# Revit family: PRD_AR_ShwrFttngsPckg_F5EShowerPanel_F5EV2008
name_source: partatom
category: Plumbing Fixtures
units: mm (PartAtom-declared; Revit-internal decimal feet)

## family parameters
Cut with Voids When Loaded = No
Enable Cutting in Views = No
Host = Face
Maintain Annotation Orientation = No
OmniClass Number = 23.45.05.14.17.11
OmniClass Title = Shower Compartments
Part Type = Normal
Room Calculation Point = No
Round Connector Dimension = Use Diameter
Shared = No

## types (1)
- F5EV2008
    AccentColour = chrome-look (glossy)
    AdditionalConnections = No
    AdjustableFlowTime = Yes
    Adjustment = No
    AssetType = Fixed
    BIMObjectName = PRD_AR_ ShowerFittingsPackage_F5EShowerPanel_F5EV2008
    BasicColour = stainless steel-look
    BodyMaterial = PRD_AR_StainlessSteel_SatinFinished
    Category = Pr_40_20_87_75, Shower fittings package
    Circulation = No
    Color = stainless steel-look
    CompatibleA3000Open = Yes
    ConnectionWithPayWaterDispenser = via electronic module
    DN = 15  [stored 0.0492126 ft]
    Default Elevation = 1200 mm
    Description = F5E - A3000 open shower panel made of stainless steel for wall mounting with straight-way valve and connecting nozzles for shower head. Electronically controlled, for connection from the rear to pre-mixed hot or cold water. Connecting nozzles for the required additional DN 15 KWC shower head with pre-fitted flow regulator 9.0 l/min. Housing made of stainless steel, single-piece enclosed, including safety screws. With solenoid valve, piezo push-button with start/stop function, waterproof electronic module, electric T-junction for connection to system cable, connecting hose with lockable water flow regulator and strainer. Activated hygiene flushing 24 hours after the last activity. With facility for parameterization, cleaning deactivation and communication via ECC2 function controller, 24 V DC.
    DiameterNominal = DN 15
    DrainSize = 15 mm  [stored 0.0492126 ft]
    Export Type to IFC As = IfcSanitaryTerminalType
    Features = For connection from the rear to pre-mixed hot or cold water. Dimensions of housing 232 x 1160 x 90 mm. Shower head must be ordered separately.
    Finish = Satin finished
    Flow = 0.2 L/s
    ForHandShower = No
    FunctionalPrinciple = Electronic self-closing
    HasTray = No
    HygieneFlushing = Yes
    IfcExportAs = IfcSanitaryTerminalType
    IfcExportType = SHOWER
    InletSize = G 1/2 A
    LockingMechanism = Top section, non-ceramic
    Manufacturer = KWC Group Management AG
    ManufacturerName = KWC Group Management AG
    ManufacturerURL = www.kwc-professional.com
    Material = stainless steel
    MaterialCasing = stainless steel
    MaterialCodeCasing = 1.4301 Chrome Nickel steel V2A
    MaterialFitting = brass-look
    MaximumFlowTime = 6500 Seconds
    MinimumFlowPressure = 1 bar
    MinimumFlowTime = 1 Seconds
    Model = F5EV2008
    ModelNumber = 2030070434
    ModelReference = F5EV2008
    NBSDescription = Shower fittings package
    NBSReference = 45-35-70/330
    Name = F5E Shower panel F5EV2008
    NominalDepth = 90 mm  [stored 0.295276 ft]
    NominalHeight = 1160 mm  [stored 3.80577 ft]
    NominalLength = 1160 mm  [stored 3.80577 ft]
    NominalWidth = 232 mm  [stored 0.761155 ft]
    OverallDepth = 90 mm
    OverallHeight = 1160 mm
    OverallWidth = 232 mm
    Parameterization = network
    PositionOfPowerConnection = from backside
    PositionOfWaterConnection = from backside
    PowerSupplyConnection = A3000 open 24 V DC
    ProductInformation = http://pim.kwc.com
    ProtectiveShutdown = Yes
    ProtectiveSystemIP = IP59K
    Push-button = Yes
    ShowerHead = for separately shower head
    ShowerPipeDraining = No
    ShowerType = Individual
    Size = 15
    SoundInsulation = No
    Status = NEW
    SurfaceFinishCasing = satin finished
    SurfaceTreatmentFitting = none
    TemperatureLimit = No
    Type IFC Predefined Type = SHOWER
    TypeOfMixing = No
    TypeOfMounting = wall mounting
    TypeOfOperation = sensor operation
    TypeOfPowerSupply = Transformer
    TypeOfSensor = piezo-electronic sensor
    TypeOfShower = shower panel
    URL = www.kwc-professional.com
    Uniclass2015Code = Pr_40_20_87_75
    Uniclass2015Title = Shower fittings package
    Uniclass2015Version = Products v1.36
    Version = 1
    VolumeFlowRateAt3Bar = 0.15 l/s
    WaterConnection = hose (gland nut)
    WithBackflowPreventer = Yes
    WithFilter = Yes
    WithRosettesCoverPlate = Yes
    WithShowerSet = No
    WithSoapDish = No
    WithTransformerPowerSupply = No

note: [stored X ft] marks values corroborated as IEEE doubles in the binary element streams (Revit-internal decimal feet)

## geometry (parser evidence)
native form markers: Sweep x5
no freeform markers — native parametric forms only
